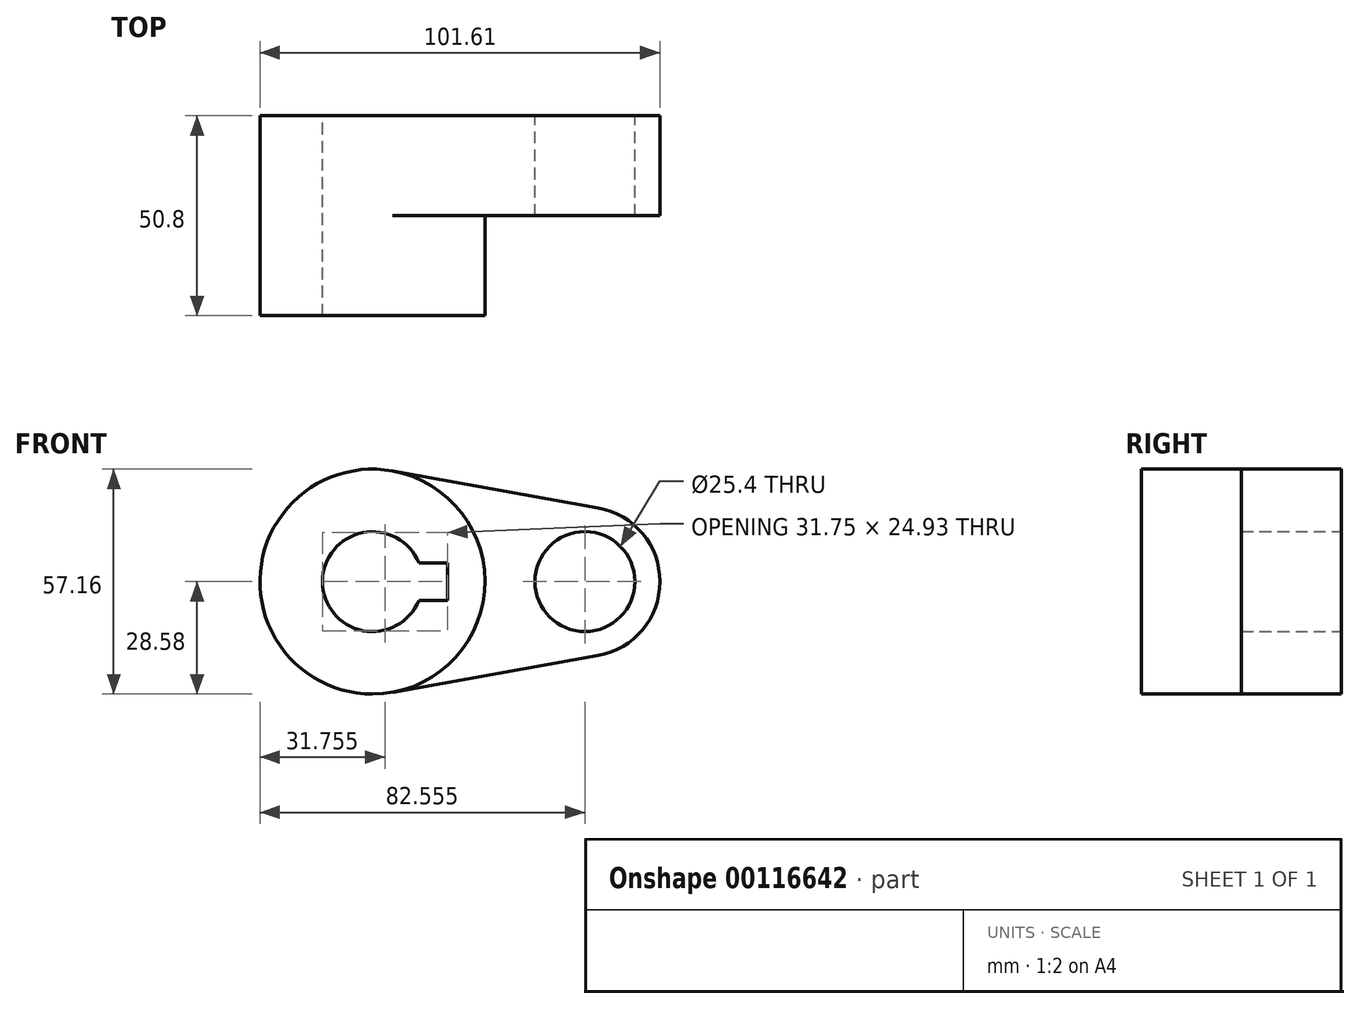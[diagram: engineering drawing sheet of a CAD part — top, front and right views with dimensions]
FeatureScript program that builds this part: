
annotation { "Feature Type Name" : "Feature", "Feature Type Description" : "" }
export const myFeature = defineFeature(function(context is Context, id is Id, definition is map)
    precondition{}
    {
        {
            var Q0;
            Q0=qCreatedBy(makeId("Front.planeOp"),FACE);
            var sketch = newSketch(context, id + "F0", { "sketchPlane" : qUnion([Q0])});
            skCircle(sketch, "E0", {"center": v(0, 0) * mm, "radius": 28.58 * mm});
            skCircle(sketch, "E1", {"center": v(53.98, 0) * mm, "radius": 19.05 * mm});
            skLineSegment(sketch, "E2", {"start": v(5.04, 28.13) * mm, "end": v(57.34, 18.75) * mm});
            skLineSegment(sketch, "E3", {"start": v(57.34, -18.75) * mm, "end": v(5.04, -28.13) * mm});
            skCircle(sketch, "E4", {"center": v(0, 0) * mm, "radius": 12.7 * mm});
            skCircle(sketch, "E5", {"center": v(53.98, 0) * mm, "radius": 12.7 * mm});
            skLineSegment(sketch, "E6.bottom", {"start": v(-19.05, 4.76) * mm, "end": v(19.05, 4.76) * mm});
            skLineSegment(sketch, "E6.top", {"start": v(-19.05, -4.76) * mm, "end": v(19.05, -4.76) * mm});
            skLineSegment(sketch, "E6.left", {"start": v(-19.05, 4.76) * mm, "end": v(-19.05, -4.76) * mm});
            skLineSegment(sketch, "E6.right", {"start": v(19.05, 4.76) * mm, "end": v(19.05, -4.76) * mm});
            skSolve(sketch);
        }
        {
            var Q0;
            {var subQ11=sQuery(id+"F0.wireOp",EDGE,"E6.left");Q0=makeQuery(id+"F0.imprint","IMPRINT",FACE,{"disambiguationData":[TD([[makeQuery(id+"F0.imprint","IMPRINT",EDGE,{"derivedFrom":subQ11}),-1.0]])]});}
            var Q1;
            {var subQ5=sQuery(id+"F0.wireOp",EDGE,"E6.left");Q1=makeQuery(id+"F0.imprint","IMPRINT",FACE,{"disambiguationData":[TD([[makeQuery(id+"F0.imprint","IMPRINT",EDGE,{"derivedFrom":subQ5}),1.0]])]});}
            var Q2;
            Q2=makeQuery(id+"F0.imprint","IMPRINT",FACE,{"disambiguationData":[TD([[makeQuery(id+"F0.imprint","IMPRINT",EDGE,{"derivedFrom":sQuery(id+"F0.wireOp",EDGE,"E5")}),-1.0]])]});
            var Q3;
            {var subQ0=sQuery(id+"F0.wireOp",EDGE,"E2");Q3=makeQuery(id+"F0.imprint","IMPRINT",FACE,{"disambiguationData":[TD([[makeQuery(id+"F0.imprint","IMPRINT",EDGE,{"derivedFrom":subQ0}),-1.0]])]});}
            extrude(context, id + "F1", {"entities" : qUnion([Q0, Q1, Q2, Q3]), "depth" : 25.4 * mm});
        }
        {
            var Q0;
            {var subQ11=sQuery(id+"F0.wireOp",EDGE,"E6.left");Q0=makeQuery(id+"F0.imprint","IMPRINT",FACE,{"disambiguationData":[TD([[makeQuery(id+"F0.imprint","IMPRINT",EDGE,{"derivedFrom":subQ11}),-1.0]])]});}
            var Q1;
            {var subQ5=sQuery(id+"F0.wireOp",EDGE,"E6.left");Q1=makeQuery(id+"F0.imprint","IMPRINT",FACE,{"disambiguationData":[TD([[makeQuery(id+"F0.imprint","IMPRINT",EDGE,{"derivedFrom":subQ5}),1.0]])]});}
            extrude(context, id + "F2", {"entities" : qUnion([Q0, Q1]), "operationType" : NewBodyOperationType.ADD, "depth" : 50.8 * mm});
        }
    });
